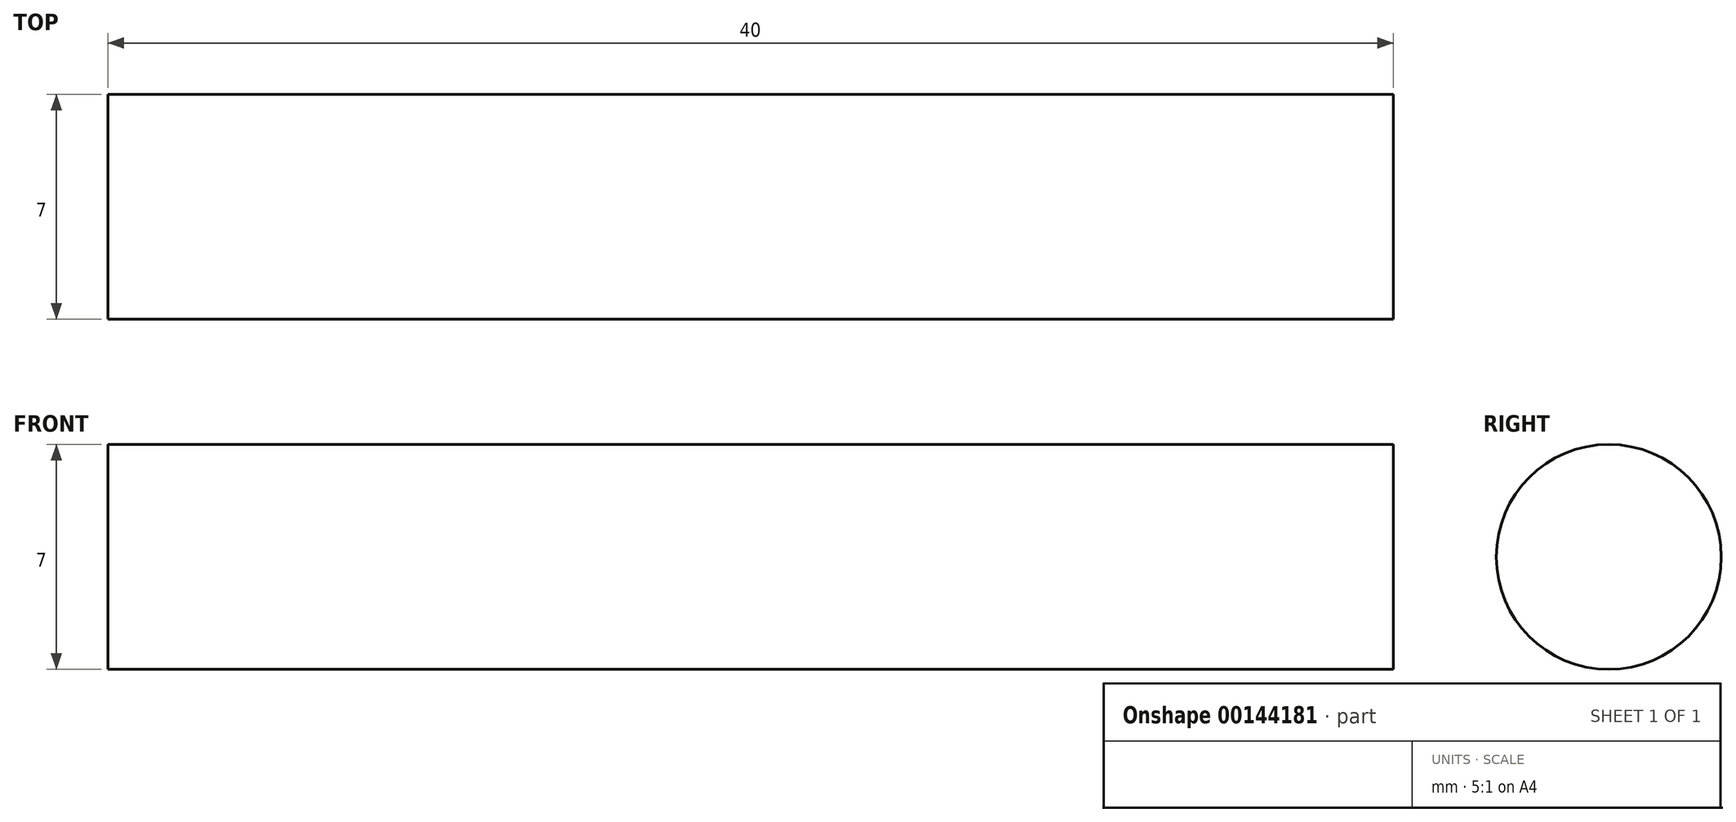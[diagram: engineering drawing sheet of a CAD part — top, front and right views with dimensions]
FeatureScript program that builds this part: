
annotation { "Feature Type Name" : "Feature", "Feature Type Description" : "" }
export const myFeature = defineFeature(function(context is Context, id is Id, definition is map)
    precondition{}
    {
        {
            var Q0;
            Q0=qCreatedBy(makeId("Right.planeOp"),FACE);
            var sketch = newSketch(context, id + "F0", { "sketchPlane" : qUnion([Q0])});
            skCircle(sketch, "E0", {"center": v(0, 0) * mm, "radius": 3.5 * mm});
            skSolve(sketch);
        }
        {
            var Q0;
            Q0=qCreatedBy(makeId("Front.planeOp"),FACE);
            var sketch = newSketch(context, id + "F1", { "sketchPlane" : qUnion([Q0])});
            skLineSegment(sketch, "E1", {"start": v(0, 0) * mm, "end": v(40, 0) * mm});
            skSolve(sketch);
        }
        {
            var Q0;
            Q0=makeQuery(id+"F0.imprint","IMPRINT",FACE,{"disambiguationData":[TD([[makeQuery(id+"F0.imprint","IMPRINT",EDGE,{"derivedFrom":sQuery(id+"F0.wireOp",EDGE,"E0")}),1.0]])]});
            var Q1;
            Q1=sQuery(id+"F1.wireOp",EDGE,"E1");
            sweep(context, id + "F2", {"profiles" : qUnion([Q0]), "path" : qUnion([Q1])});
        }
    });
